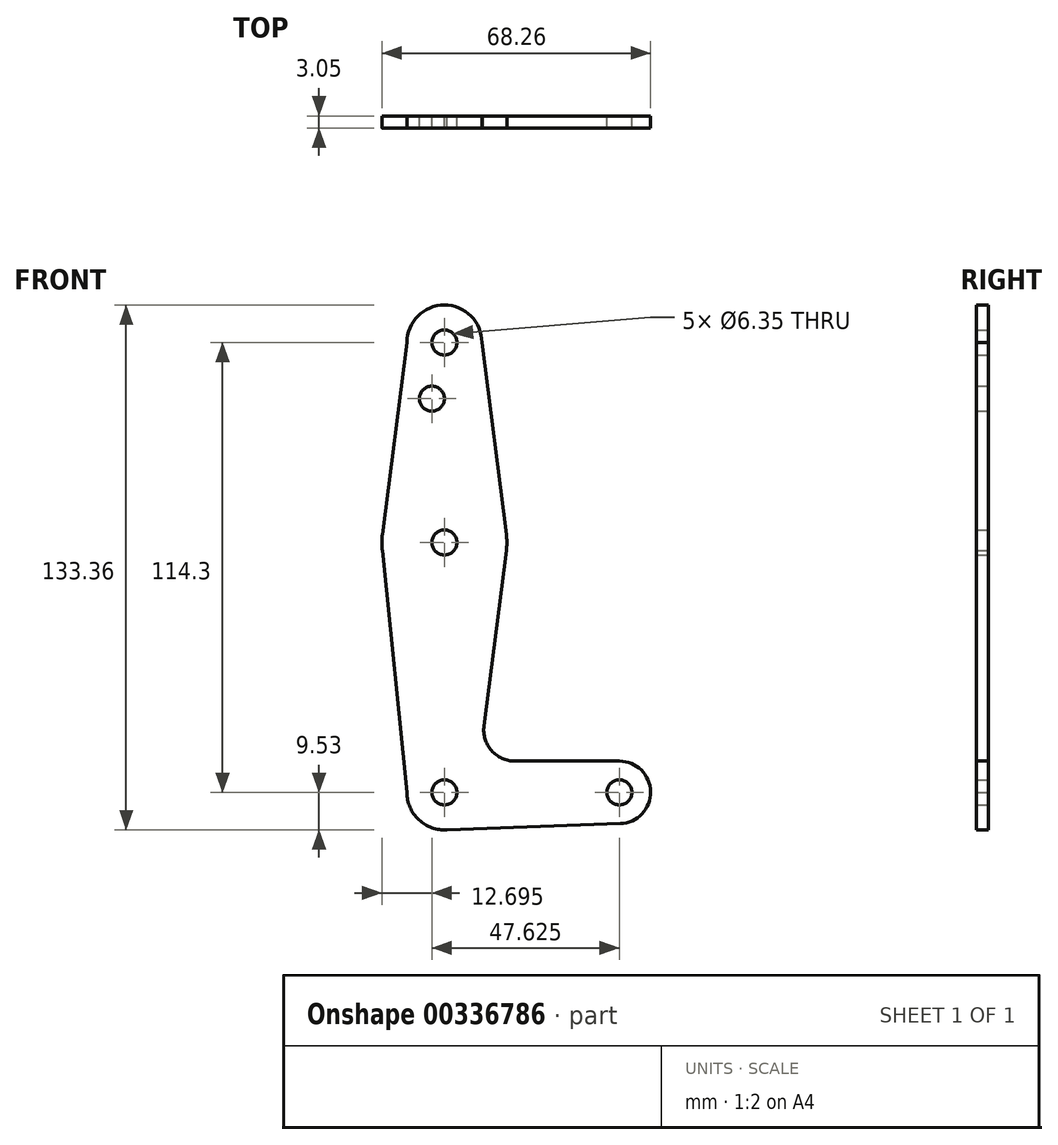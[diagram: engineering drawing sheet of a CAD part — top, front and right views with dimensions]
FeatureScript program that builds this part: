
annotation { "Feature Type Name" : "Feature", "Feature Type Description" : "" }
export const myFeature = defineFeature(function(context is Context, id is Id, definition is map)
    precondition{}
    {
        {
            var Q0;
            Q0=qCreatedBy(makeId("Front.planeOp"),FACE);
            var sketch = newSketch(context, id + "F0", { "sketchPlane" : qUnion([Q0])});
            skLineSegment(sketch, "E0", {"start": v(0, 0) * mm, "end": v(0, 114.3) * mm});
            skLineSegment(sketch, "E1", {"start": v(0, 0) * mm, "end": v(44.45, 0) * mm});
            skCircle(sketch, "E2", {"center": v(0, 0) * mm, "radius": 9.53 * mm});
            skCircle(sketch, "E3", {"center": v(44.45, 0) * mm, "radius": 7.94 * mm});
            skCircle(sketch, "E4", {"center": v(0, 114.3) * mm, "radius": 9.53 * mm});
            skCircle(sketch, "E5", {"center": v(0, 63.5) * mm, "radius": 15.88 * mm});
            skLineSegment(sketch, "E6", {"start": v(-9.53, 114.3) * mm, "end": v(-15.75, 65.5) * mm});
            skLineSegment(sketch, "E7", {"start": v(0, -9.53) * mm, "end": v(44.75, -7.93) * mm});
            skCircle(sketch, "E8", {"center": v(-3.18, 100.03) * mm, "radius": 3.18 * mm});
            skCircle(sketch, "E9", {"center": v(0, 63.5) * mm, "radius": 3.18 * mm});
            skCircle(sketch, "E10", {"center": v(0, 114.3) * mm, "radius": 3.18 * mm});
            skCircle(sketch, "E11", {"center": v(0, 0) * mm, "radius": 3.18 * mm});
            skCircle(sketch, "E12", {"center": v(44.45, 0) * mm, "radius": 3.18 * mm});
            skLineSegment(sketch, "E13", {"start": v(9.53, 114.3) * mm, "end": v(15.75, 65.5) * mm});
            skLineSegment(sketch, "E14", {"start": v(-15.75, 61.5) * mm, "end": v(-9.52, 0) * mm});
            skLineSegment(sketch, "E15", {"start": v(10.06, 16.9) * mm, "end": v(15.75, 61.5) * mm});
            skLineSegment(sketch, "E16", {"start": v(17.95, 7.94) * mm, "end": v(44.45, 7.94) * mm});
            skPoint(sketch, "E17.newPointB", {"position": v(0, 7.94) * mm});
            skArc(sketch, "E17.filletArc", {"start": v(10.06, 16.9) * mm, "mid": v(11.98, 10.63) * mm, "end": v(17.95, 7.94) * mm});
            skSolve(sketch);
        }
        {
            var Q0;
            Q0 = qSketchRegion(id + "F0", true);
            var Q1;
            {var subQ0=sQuery(id+"F0.wireOp",EDGE,"E11");var subQ1=sQuery(id+"F0.wireOp",EDGE,"E0");var subQ2=makeQuery(id+"F0.imprint","INTERSECT",VERTEX,{"derivedFrom":[subQ1,subQ0]});Q1=makeQuery(id+"F0.imprint","IMPRINT",FACE,{"disambiguationData":[TD([[makeQuery(id+"F0.imprint","IMPRINT",EDGE,{"disambiguationData":[TD([[subQ2,-1.0]])],"derivedFrom":subQ1}),-1.0]])]});}
            extrude(context, id + "F1", {"entities" : qUnion([Q0, Q1]), "depth" : 3.05 * mm});
        }
    });
